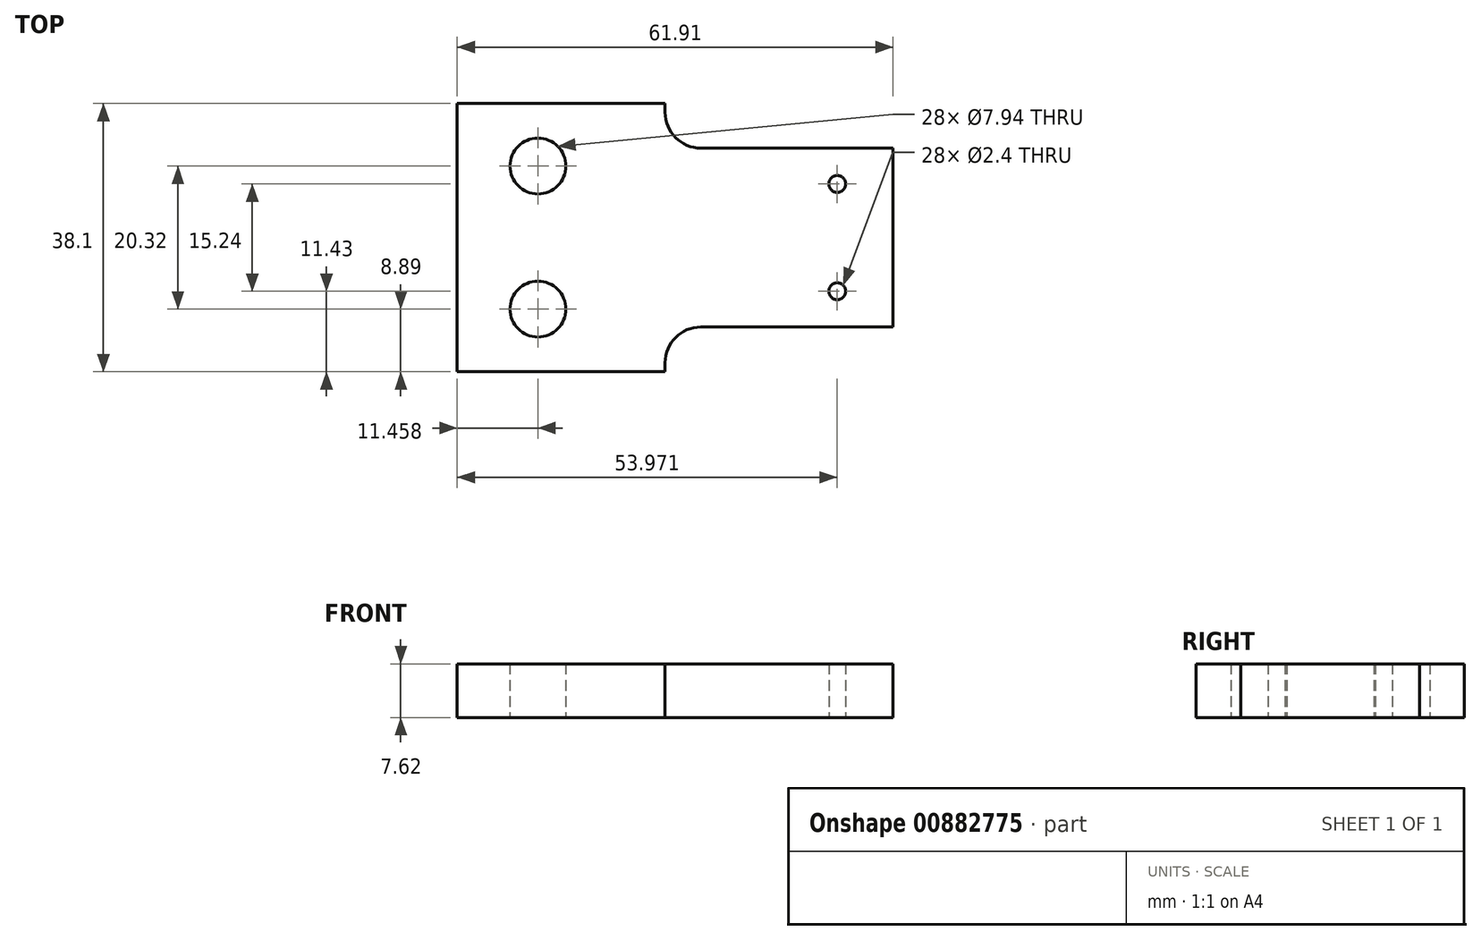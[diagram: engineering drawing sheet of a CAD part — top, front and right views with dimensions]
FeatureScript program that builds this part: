
annotation { "Feature Type Name" : "Feature", "Feature Type Description" : "" }
export const myFeature = defineFeature(function(context is Context, id is Id, definition is map)
    precondition{}
    {
        {
            var Q0;
            Q0=qCreatedBy(makeId("Top.planeOp"),FACE);
            var sketch = newSketch(context, id + "F0", { "sketchPlane" : qUnion([Q0])});
            skLineSegment(sketch, "E0.bottom", {"start": v(-14.76, 19.05) * mm, "end": v(14.76, 19.05) * mm});
            skLineSegment(sketch, "E0.top", {"start": v(-14.76, -19.05) * mm, "end": v(14.76, -19.05) * mm});
            skLineSegment(sketch, "E0.left", {"start": v(-14.76, 19.05) * mm, "end": v(-14.76, -19.05) * mm});
            skLineSegment(sketch, "E0.right", {"start": v(14.76, 19.05) * mm, "end": v(14.76, 12.7) * mm});
            skPoint(sketch, "E0.middle", {"position": v(0, 0) * mm});
            skLineSegment(sketch, "E1.bottom", {"start": v(14.76, 12.7) * mm, "end": v(47.15, 12.7) * mm});
            skLineSegment(sketch, "E1.top", {"start": v(14.76, -12.7) * mm, "end": v(47.15, -12.7) * mm});
            skLineSegment(sketch, "E1.left", {"start": v(-14.76, 12.7) * mm, "end": v(-14.76, -12.7) * mm});
            skLineSegment(sketch, "E1.right", {"start": v(47.15, 12.7) * mm, "end": v(47.15, -12.7) * mm});
            skCircle(sketch, "E2", {"center": v(-3.3, -10.16) * mm, "radius": 3.97 * mm});
            skCircle(sketch, "E3", {"center": v(-3.3, 10.16) * mm, "radius": 3.97 * mm});
            skLineSegment(sketch, "E4.trimOffspring", {"start": v(14.76, -12.7) * mm, "end": v(14.76, -19.05) * mm});
            skCircle(sketch, "E5", {"center": v(39.21, 7.62) * mm, "radius": 1.2 * mm});
            skCircle(sketch, "E6", {"center": v(39.21, -7.62) * mm, "radius": 1.2 * mm});
            skSolve(sketch);
        }
        {
            var Q0;
            Q0 = qSketchRegion(id + "F0", true);
            extrude(context, id + "F1", {"entities" : qUnion([Q0]), "depth" : 7.62 * mm, "offsetDistance" : 25.4 * mm});
        }
        {
            var Q0;
            Q0=makeQuery(id+"Fa5leIqCe889qlM_1.boolean.opBoolean","COPY",EDGE,{"derivedFrom":makeQuery(id+"Fa5leIqCe889qlM_1.opExtrude","SWEPT_EDGE",EDGE,{"disambiguationData":[OSD([sQuery(id+"F0.wireOp",EDGE,"E1.top"),sQuery(id+"F0.wireOp",EDGE,"E4.trimOffspring"),sQuery(id+"FD8B3fhHg46P8mS_1.wireOp",EDGE,"hjla6CkC-rRQL-1TCw-tlu4-94vFBVHXmVHE.top"),sQuery(id+"FD8B3fhHg46P8mS_1.wireOp",EDGE,"hjla6CkC-rRQL-1TCw-tlu4-94vFBVHXmVHE.right")])]})});
            var Q1;
            Q1=makeQuery(id+"F1.opExtrude","SWEPT_EDGE",EDGE,{"disambiguationData":[OSD([sQuery(id+"F0.wireOp",EDGE,"E1.top"),sQuery(id+"F0.wireOp",EDGE,"E4.trimOffspring")])]});
            var Q2;
            Q2=makeQuery(id+"F1.opExtrude","SWEPT_EDGE",EDGE,{"disambiguationData":[OSD([sQuery(id+"F0.wireOp",EDGE,"E0.right"),sQuery(id+"F0.wireOp",EDGE,"E1.bottom")])]});
            fillet(context, id + "F2", {"entities" : qUnion([Q0, Q1, Q2]), "radius" : 5.08 * mm, "tangentPropagation" : true, "allowEdgeOverflow" : false});
        }
    });
